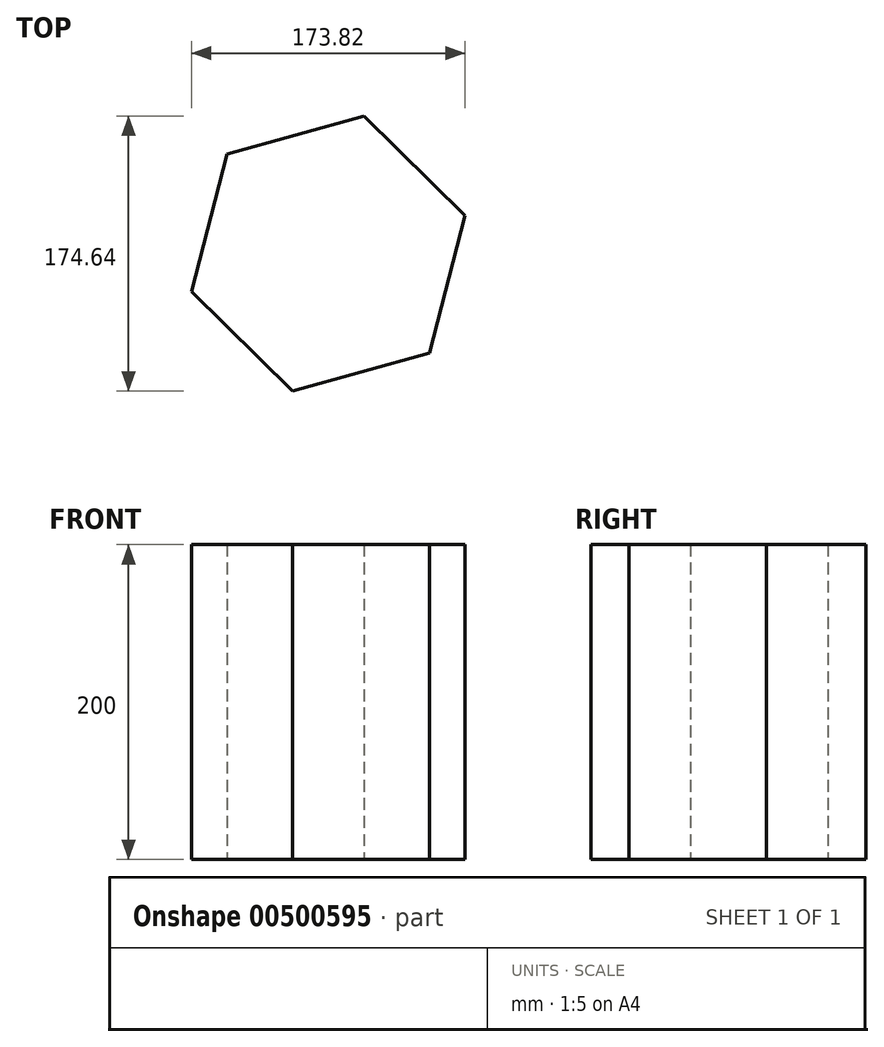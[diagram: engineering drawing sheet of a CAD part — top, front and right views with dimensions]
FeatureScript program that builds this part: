
annotation { "Feature Type Name" : "Feature", "Feature Type Description" : "" }
export const myFeature = defineFeature(function(context is Context, id is Id, definition is map)
    precondition{}
    {
        {
            var Q0;
            Q0=qCreatedBy(makeId("Top.planeOp"),FACE);
            var sketch = newSketch(context, id + "F0", { "sketchPlane" : qUnion([Q0])});
            skCircle(sketch, "E0.cCircle", {"center": v(0, 0) * mm, "radius": 90.2 * mm, "construction": true});
            skLineSegment(sketch, "E0.0", {"start": v(64.33, -63.22) * mm, "end": v(-22.58, -87.32) * mm});
            skLineSegment(sketch, "E0.1", {"start": v(-22.58, -87.32) * mm, "end": v(-86.91, -24.1) * mm});
            skLineSegment(sketch, "E0.2", {"start": v(-86.91, -24.1) * mm, "end": v(-64.33, 63.22) * mm});
            skLineSegment(sketch, "E0.3", {"start": v(-64.33, 63.22) * mm, "end": v(22.58, 87.32) * mm});
            skLineSegment(sketch, "E0.4", {"start": v(22.58, 87.32) * mm, "end": v(86.91, 24.1) * mm});
            skLineSegment(sketch, "E0.5", {"start": v(86.91, 24.1) * mm, "end": v(64.33, -63.22) * mm});
            skSolve(sketch);
        }
        {
            var Q0;
            Q0=makeQuery(id+"F0.imprint","IMPRINT",FACE,{"disambiguationData":[TD([[makeQuery(id+"F0.imprint","IMPRINT",EDGE,{"derivedFrom":sQuery(id+"F0.wireOp",EDGE,"E0.0")}),-1.0]])]});
            extrude(context, id + "F1", {"entities" : qUnion([Q0]), "depth" : 200 * mm});
        }
    });
